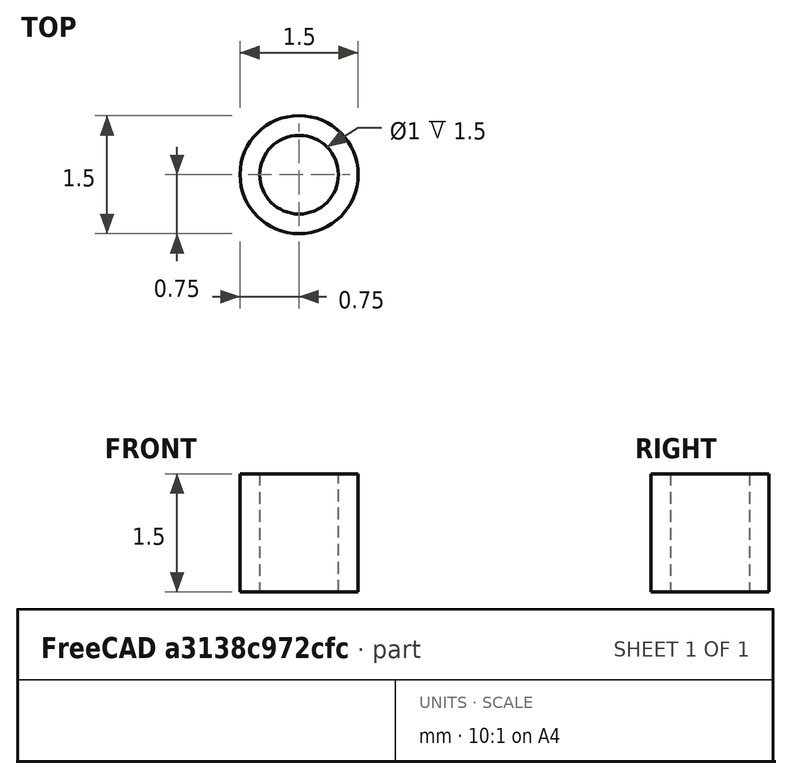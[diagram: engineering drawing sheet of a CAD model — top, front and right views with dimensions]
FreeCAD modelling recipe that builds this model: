
FCSTD DOCUMENT  (FreeCAD 0.19R24291 (Git))
Label: screw01
License: All rights reserved
LicenseURL: http://en.wikipedia.org/wiki/All_rights_reserved
objects: Spreadsheet::Sheet×1, Sketcher::SketchObject×1, PartDesign::Pad×1, PartDesign::Body×1
note: 4 computed .brp shape members not serialized (recipe doc carries the construction recipe); baked Part::Feature solids carry a one-line shape summary decoded from their .brp

FEATURE [Spreadsheet::Sheet] Spreadsheet
  cells = B2=screw; B3=rad; C3(sw_r)=0.75; B4=h; C4(sw_h)=1.5; B5=hole; C5(sw_hl)=0.5
FEATURE [Sketcher::SketchObject] Sketch
  FullyConstrained = true
  MapMode = 5
  Support = -> [XY_Plane]
  expr: Constraints[3] = Spreadsheet.sw_hl
  expr: Constraints[2] = Spreadsheet.sw_r
  sketch-geometry (2):
    g0: Circle CenterX=0 CenterY=0 CenterZ=0 NormalX=0 NormalY=0 NormalZ=1 AngleXU=0 Radius=0.75
    g1: Circle CenterX=0 CenterY=0 CenterZ=0 NormalX=0 NormalY=0 NormalZ=1 AngleXU=0 Radius=0.5
  constraints (4):
    c: Coincident(g0,g-1)
    c: Coincident(g1,g0)
    c: Radius(g0) = 0.75
    c: Radius(g1) = 0.5
FEATURE [PartDesign::Pad] Pad
  Direction = (1,1,1)
  Length = 1.5
  Length2 = 100
  Profile = -> Sketch
  Type = 0
  expr: Length = Spreadsheet.sw_h
FEATURE [PartDesign::Body] Body
  Group = -> [Sketch,Pad]
  Origin = -> Origin
  Tip = -> Pad
